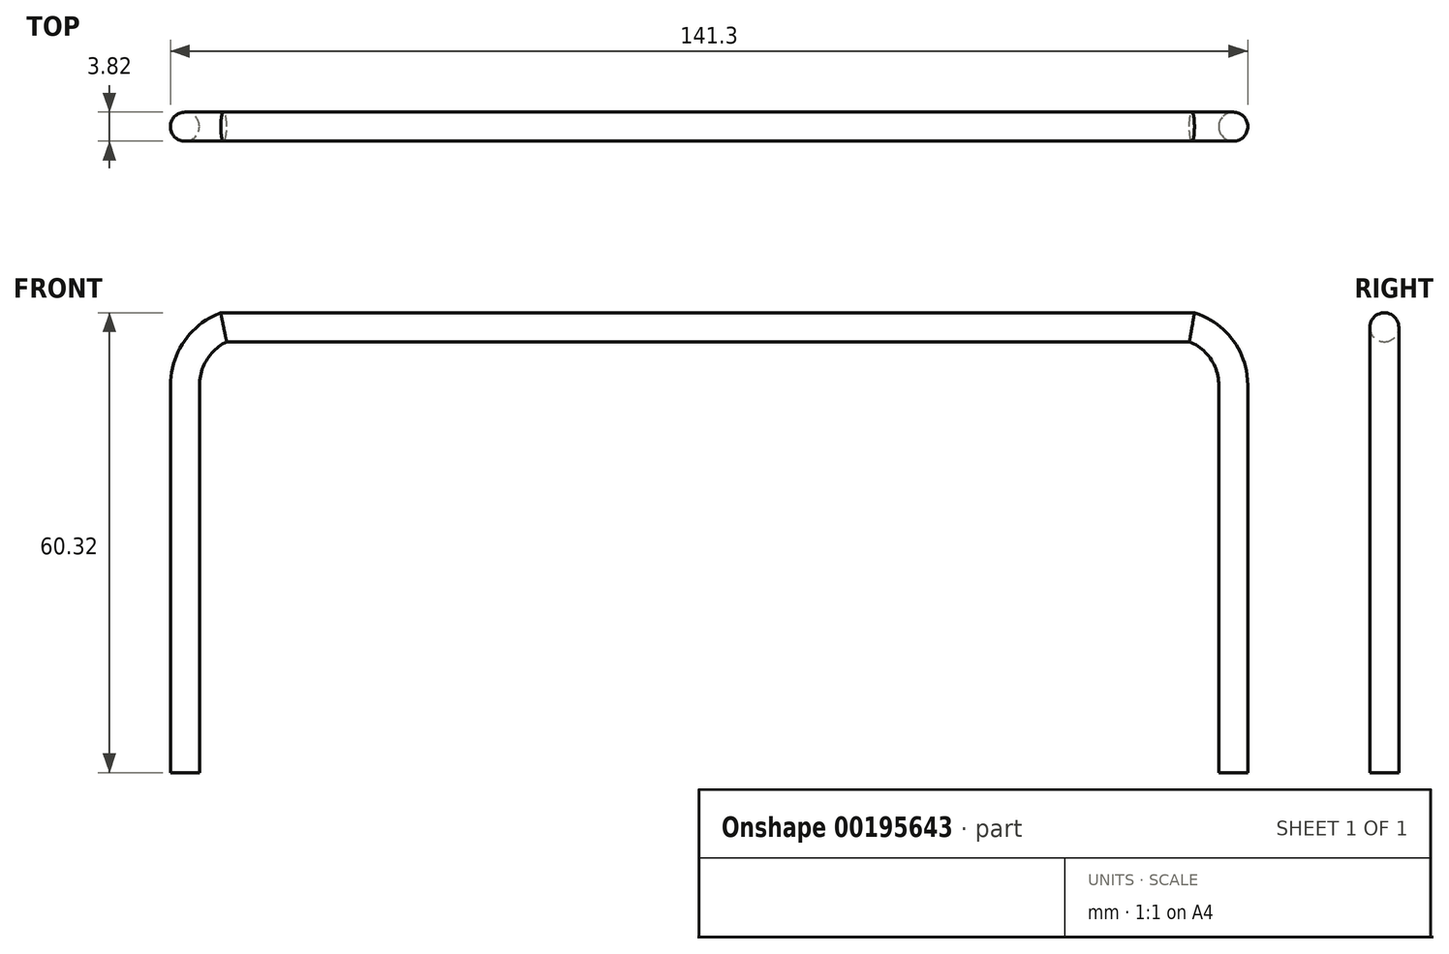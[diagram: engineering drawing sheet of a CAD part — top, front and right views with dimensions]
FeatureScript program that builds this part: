
annotation { "Feature Type Name" : "Feature", "Feature Type Description" : "" }
export const myFeature = defineFeature(function(context is Context, id is Id, definition is map)
    precondition{}
    {
        {
            var Q0;
            Q0=qCreatedBy(makeId("Front.planeOp"),FACE);
            var sketch = newSketch(context, id + "F0", { "sketchPlane" : qUnion([Q0])});
            skLineSegment(sketch, "E0", {"start": v(-68.57, 0) * mm, "end": v(-68.57, 50.8) * mm});
            skLineSegment(sketch, "E1", {"start": v(68.92, 0) * mm, "end": v(68.92, 50.8) * mm});
            skLineSegment(sketch, "E2", {"start": v(-63.5, 58.42) * mm, "end": v(0, 58.42) * mm});
            skLineSegment(sketch, "E3", {"start": v(0, 58.42) * mm, "end": v(63.5, 58.42) * mm});
            skArc(sketch, "E4", {"start": v(-68.57, 50.8) * mm, "mid": v(-67.19, 55.38) * mm, "end": v(-63.5, 58.42) * mm});
            skArc(sketch, "E5", {"start": v(68.92, 50.8) * mm, "mid": v(67.43, 55.48) * mm, "end": v(63.5, 58.42) * mm});
            skSolve(sketch);
        }
        {
            var Q0;
            Q0=qCreatedBy(makeId("Top.planeOp"),FACE);
            var sketch = newSketch(context, id + "F1", { "sketchPlane" : qUnion([Q0])});
            skCircle(sketch, "E6", {"center": v(-68.57, 0) * mm, "radius": 1.9 * mm});
            skSolve(sketch);
        }
        {
            var Q0;
            Q0=makeQuery(id+"F1.imprint","IMPRINT",FACE,{"disambiguationData":[TD([[makeQuery(id+"F1.imprint","IMPRINT",EDGE,{"derivedFrom":sQuery(id+"F1.wireOp",EDGE,"E6")}),1.0]])]});
            var Q1;
            Q1 = qConstructionFilter(qBodyType(qCreatedBy(id + "F0" ,EDGE), BodyType.WIRE), ConstructionObject.NO);
            sweep(context, id + "F2", {"profiles" : qUnion([Q0]), "path" : qUnion([Q1])});
        }
    });
